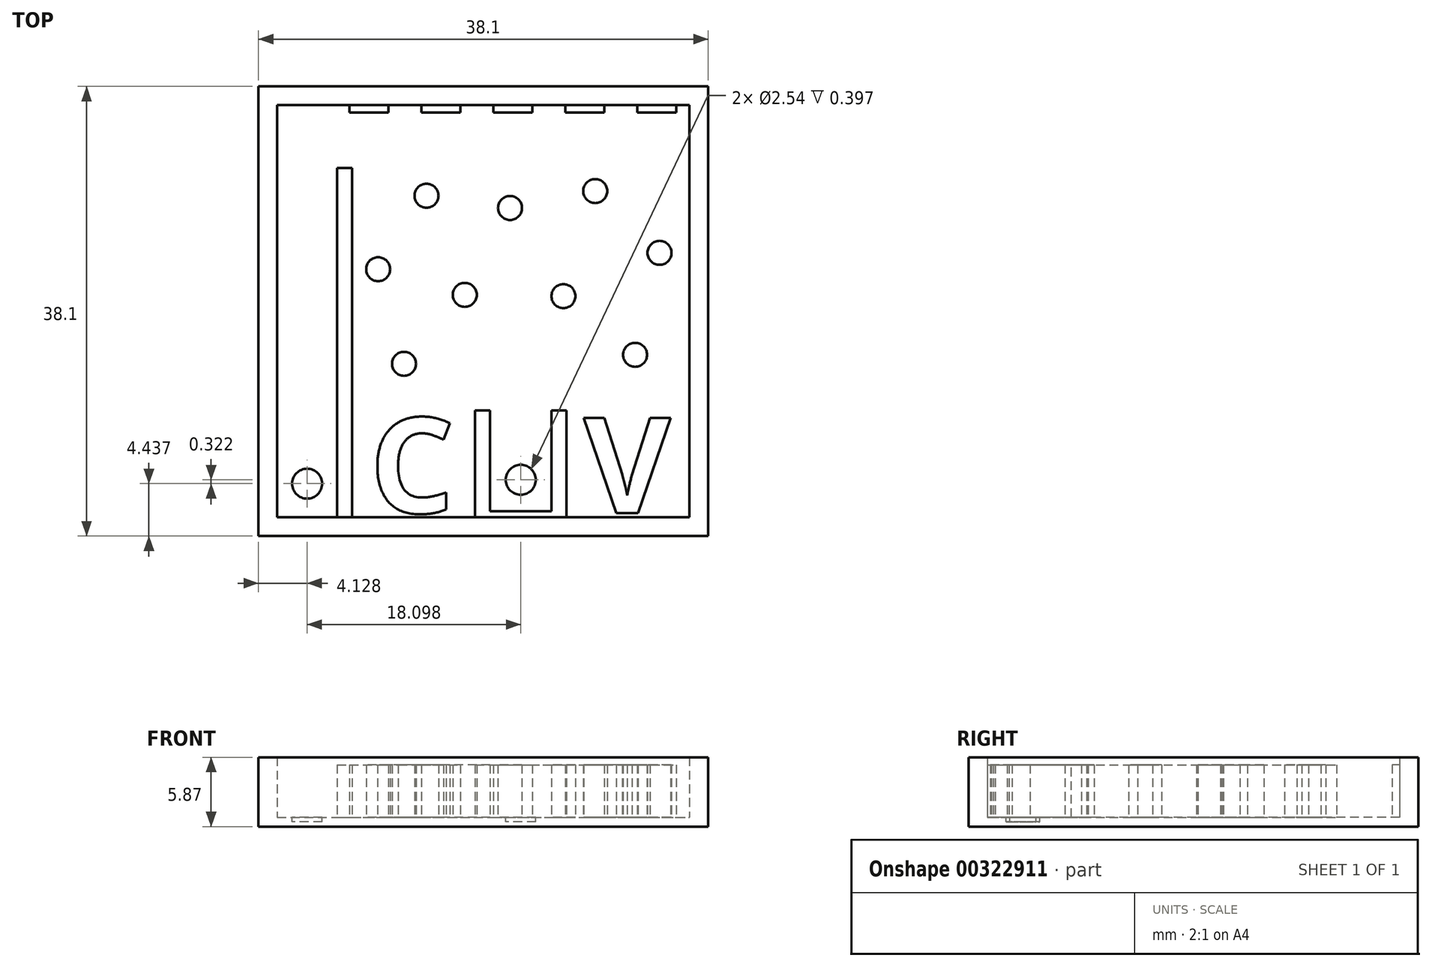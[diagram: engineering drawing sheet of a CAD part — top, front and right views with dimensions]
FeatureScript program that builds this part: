
annotation { "Feature Type Name" : "Feature", "Feature Type Description" : "" }
export const myFeature = defineFeature(function(context is Context, id is Id, definition is map)
    precondition{}
    {
        {
            var Q0;
            Q0=qCreatedBy(makeId("Top.planeOp"),FACE);
            var sketch = newSketch(context, id + "F0", { "sketchPlane" : qUnion([Q0])});
            skLineSegment(sketch, "E0.bottom", {"start": v(-19.05, 22.12) * mm, "end": v(19.05, 22.12) * mm});
            skLineSegment(sketch, "E0.top", {"start": v(-19.05, -15.98) * mm, "end": v(19.05, -15.98) * mm});
            skLineSegment(sketch, "E0.left", {"start": v(-19.05, 22.12) * mm, "end": v(-19.05, -15.98) * mm});
            skLineSegment(sketch, "E0.right", {"start": v(19.05, 22.12) * mm, "end": v(19.05, -15.98) * mm});
            skSolve(sketch);
        }
        {
            var Q0;
            Q0=makeQuery(id+"F0.imprint","IMPRINT",FACE,{"disambiguationData":[TD([[makeQuery(id+"F0.imprint","IMPRINT",EDGE,{"derivedFrom":sQuery(id+"F0.wireOp",EDGE,"E0.bottom")}),-1.0]])]});
            extrude(context, id + "F1", {"entities" : qUnion([Q0]), "depth" : 0.8 * mm});
        }
        {
            var Q0;
            Q0=makeQuery(id+"F1.opExtrude","CAP_FACE",FACE,{"disambiguationData":[OSD([sQuery(id+"F0.wireOp",EDGE,"E0.bottom"),sQuery(id+"F0.wireOp",EDGE,"E0.top"),sQuery(id+"F0.wireOp",EDGE,"E0.left"),sQuery(id+"F0.wireOp",EDGE,"E0.right")])],"isStart":false});
            var sketch = newSketch(context, id + "F2", { "sketchPlane" : qUnion([Q0])});
            skLineSegment(sketch, "E1.0", {"start": v(-17.46, 20.53) * mm, "end": v(17.46, 20.53) * mm});
            skLineSegment(sketch, "E1.1", {"start": v(-17.46, 20.53) * mm, "end": v(-17.46, -14.4) * mm});
            skLineSegment(sketch, "E1.2", {"start": v(-17.46, -14.4) * mm, "end": v(17.46, -14.4) * mm});
            skLineSegment(sketch, "E1.3", {"start": v(17.46, 20.53) * mm, "end": v(17.46, -14.4) * mm});
            skSolve(sketch);
        }
        {
            var Q0;
            Q0=makeQuery(id+"F2.imprint","IMPRINT",FACE,{"disambiguationData":[TD([[makeQuery(id+"F2.imprint","IMPRINT",EDGE,{"derivedFrom":sQuery(id+"F2.wireOp",EDGE,"E1.0")}),1.0]])]});
            extrude(context, id + "F3", {"entities" : qUnion([Q0]), "operationType" : NewBodyOperationType.ADD, "depth" : 5.08 * mm});
        }
        {
            var Q0;
            Q0=makeQuery(id+"F1.opExtrude","CAP_FACE",FACE,{"disambiguationData":[OSD([sQuery(id+"F0.wireOp",EDGE,"E0.bottom"),sQuery(id+"F0.wireOp",EDGE,"E0.top"),sQuery(id+"F0.wireOp",EDGE,"E0.left"),sQuery(id+"F0.wireOp",EDGE,"E0.right")])],"isStart":false});
            var sketch = newSketch(context, id + "F4", { "sketchPlane" : qUnion([Q0])});
            skLineSegment(sketch, "E2.bottom", {"start": v(-12.38, -14.4) * mm, "end": v(-11.11, -14.4) * mm});
            skLineSegment(sketch, "E2.top", {"start": v(-12.38, 15.2) * mm, "end": v(-11.11, 15.2) * mm});
            skLineSegment(sketch, "E2.left", {"start": v(-12.38, -14.4) * mm, "end": v(-12.38, 15.2) * mm});
            skLineSegment(sketch, "E2.right", {"start": v(-11.11, -14.4) * mm, "end": v(-11.11, 15.2) * mm});
            skLineSegment(sketch, "E3", {"start": v(-17.46, -14.4) * mm, "end": v(-12.38, -14.4) * mm});
            skCircle(sketch, "E4", {"center": v(-14.92, -11.54) * mm, "radius": 1.27 * mm});
            skPoint(sketch, "E4.centerSnap0", {"position": v(-14.92, -14.4) * mm});
            skLineSegment(sketch, "E5.bottom", {"start": v(0.85, 20.53) * mm, "end": v(4.15, 20.53) * mm});
            skLineSegment(sketch, "E5.top", {"start": v(0.85, 19.9) * mm, "end": v(4.15, 19.9) * mm});
            skLineSegment(sketch, "E5.left", {"start": v(0.85, 20.53) * mm, "end": v(0.85, 19.9) * mm});
            skLineSegment(sketch, "E5.right", {"start": v(4.15, 20.53) * mm, "end": v(4.15, 19.9) * mm});
            skLineSegment(sketch, "E6.bottom", {"start": v(-5.24, 20.53) * mm, "end": v(-1.94, 20.53) * mm});
            skLineSegment(sketch, "E6.top", {"start": v(-5.24, 19.9) * mm, "end": v(-1.94, 19.9) * mm});
            skLineSegment(sketch, "E6.left", {"start": v(-5.24, 20.53) * mm, "end": v(-5.24, 19.9) * mm});
            skLineSegment(sketch, "E6.right", {"start": v(-1.94, 20.53) * mm, "end": v(-1.94, 19.9) * mm});
            skLineSegment(sketch, "E7.bottom", {"start": v(6.95, 20.53) * mm, "end": v(10.25, 20.53) * mm});
            skLineSegment(sketch, "E7.top", {"start": v(6.95, 19.9) * mm, "end": v(10.25, 19.9) * mm});
            skLineSegment(sketch, "E7.left", {"start": v(6.95, 20.53) * mm, "end": v(6.95, 19.9) * mm});
            skLineSegment(sketch, "E7.right", {"start": v(10.25, 20.53) * mm, "end": v(10.25, 19.9) * mm});
            skLineSegment(sketch, "E8.bottom", {"start": v(13.04, 20.53) * mm, "end": v(16.35, 20.53) * mm});
            skLineSegment(sketch, "E8.top", {"start": v(13.04, 19.9) * mm, "end": v(16.35, 19.9) * mm});
            skLineSegment(sketch, "E8.left", {"start": v(13.04, 20.53) * mm, "end": v(13.04, 19.9) * mm});
            skLineSegment(sketch, "E8.right", {"start": v(16.35, 20.53) * mm, "end": v(16.35, 19.9) * mm});
            skLineSegment(sketch, "E9.bottom", {"start": v(-11.34, 20.53) * mm, "end": v(-8.04, 20.53) * mm});
            skLineSegment(sketch, "E9.top", {"start": v(-11.34, 19.9) * mm, "end": v(-8.04, 19.9) * mm});
            skLineSegment(sketch, "E9.left", {"start": v(-11.34, 20.53) * mm, "end": v(-11.34, 19.9) * mm});
            skLineSegment(sketch, "E9.right", {"start": v(-8.04, 20.53) * mm, "end": v(-8.04, 19.9) * mm});
            skText(sketch, "E10", { "text": "C", "fontName": "OpenSans-Bold.ttf"});
            skText(sketch, "E11", { "text": "V", "fontName": "OpenSans-Bold.ttf"});
            skPoint(sketch, "E12.endSnap0", {"position": v(0, -14.4) * mm});
            skLineSegment(sketch, "E13.bottom", {"start": v(5.78, -14.4) * mm, "end": v(7.05, -14.4) * mm});
            skLineSegment(sketch, "E13.top", {"start": v(5.78, -5.33) * mm, "end": v(7.05, -5.33) * mm});
            skLineSegment(sketch, "E13.left", {"start": v(5.78, -14.4) * mm, "end": v(5.78, -5.33) * mm});
            skLineSegment(sketch, "E13.right", {"start": v(7.05, -14.4) * mm, "end": v(7.05, -5.33) * mm});
            skCircle(sketch, "E14", {"center": v(3.18, -11.22) * mm, "radius": 1.27 * mm});
            skCircle(sketch, "E15", {"center": v(-4.81, 12.85) * mm, "radius": 1.02 * mm});
            skCircle(sketch, "E16", {"center": v(2.27, 11.82) * mm, "radius": 1.02 * mm});
            skCircle(sketch, "E17", {"center": v(9.48, 13.25) * mm, "radius": 1.02 * mm});
            skCircle(sketch, "E18", {"center": v(14.93, 8.01) * mm, "radius": 1.02 * mm});
            skCircle(sketch, "E19", {"center": v(-8.9, 6.63) * mm, "radius": 1.02 * mm});
            skCircle(sketch, "E20", {"center": v(-1.57, 4.46) * mm, "radius": 1.02 * mm});
            skCircle(sketch, "E21", {"center": v(6.79, 4.34) * mm, "radius": 1.02 * mm});
            skLineSegment(sketch, "E22.bottom", {"start": v(0.57, -5.33) * mm, "end": v(-0.7, -5.33) * mm});
            skLineSegment(sketch, "E22.top", {"start": v(0.57, -14.4) * mm, "end": v(-0.7, -14.4) * mm});
            skLineSegment(sketch, "E22.left", {"start": v(0.57, -5.33) * mm, "end": v(0.57, -14.4) * mm});
            skLineSegment(sketch, "E22.right", {"start": v(-0.7, -5.33) * mm, "end": v(-0.7, -14.4) * mm});
            skLineSegment(sketch, "E23.bottom", {"start": v(0.57, -14.4) * mm, "end": v(5.78, -14.4) * mm});
            skLineSegment(sketch, "E23.top", {"start": v(0.57, -13.89) * mm, "end": v(5.78, -13.89) * mm});
            skLineSegment(sketch, "E23.left", {"start": v(0.57, -14.4) * mm, "end": v(0.57, -13.89) * mm});
            skLineSegment(sketch, "E23.right", {"start": v(5.78, -14.4) * mm, "end": v(5.78, -13.89) * mm});
            skCircle(sketch, "E24", {"center": v(12.86, -0.63) * mm, "radius": 1.02 * mm});
            skPoint(sketch, "E25.endSnap0", {"position": v(14.7, 19.9) * mm});
            skCircle(sketch, "E26", {"center": v(-6.72, -1.4) * mm, "radius": 1.02 * mm});
            const initialGuessF4  = {"E10": [-0.00963, -0.01403, 1, 0, 0.00813], "E11": [0.00852, -0.01403, 1, 0, 0.00813]};
            skSetInitialGuess(sketch, initialGuessF4);
            skSolve(sketch);
        }
        {
            var Q0;
            Q0=makeQuery(id+"F4.imprint","IMPRINT",FACE,{"disambiguationData":[TD([[makeQuery(id+"F4.imprint","IMPRINT",EDGE,{"derivedFrom":sQuery(id+"F4.wireOp",EDGE,"E4")}),1.0]])]});
            var Q1;
            Q1=makeQuery(id+"F4.imprint","IMPRINT",FACE,{"disambiguationData":[TD([[makeQuery(id+"F4.imprint","IMPRINT",EDGE,{"derivedFrom":sQuery(id+"F4.wireOp",EDGE,"E14")}),1.0]])]});
            var Q2;
            {var subQ0=sQuery(id+"F4.wireOp",EDGE,"E14");var subQ1=sQuery(id+"F4.wireOp",EDGE,"E12");var subQ2=makeQuery(id+"F4.imprint","INTERSECT",VERTEX,{"disambiguationData":[OD(0.0)],"derivedFrom":[subQ1,subQ0]});Q2=makeQuery(id+"F4.imprint","IMPRINT",FACE,{"disambiguationData":[TD([[makeQuery(id+"F4.imprint","IMPRINT",EDGE,{"disambiguationData":[TD([[subQ2,-1.0]])],"derivedFrom":subQ1}),1.0]])]});}
            var Q3;
            {var subQ0=sQuery(id+"F4.wireOp",EDGE,"E14");var subQ1=sQuery(id+"F4.wireOp",EDGE,"Font8BTO-rPXh-HUv9-cvXY-GG9v0Sla35Q1");var subQ2=makeQuery(id+"F4.imprint","INTERSECT",VERTEX,{"disambiguationData":[OD(0.0)],"derivedFrom":[subQ1,subQ0]});Q3=makeQuery(id+"F4.imprint","IMPRINT",FACE,{"disambiguationData":[TD([[makeQuery(id+"F4.imprint","IMPRINT",EDGE,{"disambiguationData":[TD([[subQ2,-1.0]])],"derivedFrom":subQ1}),1.0]])]});}
            extrude(context, id + "F5", {"entities" : qUnion([Q0, Q1, Q2, Q3]), "operationType" : NewBodyOperationType.REMOVE, "oppositeDirection" : true, "depth" : 0.4 * mm});
        }
        {
            var Q0;
            Q0=makeQuery(id+"F4.imprint","IMPRINT",FACE,{"disambiguationData":[TD([[makeQuery(id+"F4.imprint","IMPRINT",EDGE,{"derivedFrom":sQuery(id+"F4.wireOp",EDGE,"E2.bottom")}),1.0]])]});
            var Q1;
            Q1=makeQuery(id+"F4.imprint","IMPRINT",FACE,{"disambiguationData":[TD([[makeQuery(id+"F4.imprint","IMPRINT",EDGE,{"derivedFrom":sQuery(id+"F4.wireOp",EDGE,"E9.bottom")}),-1.0]])]});
            var Q2;
            Q2=makeQuery(id+"F4.imprint","IMPRINT",FACE,{"disambiguationData":[TD([[makeQuery(id+"F4.imprint","IMPRINT",EDGE,{"derivedFrom":sQuery(id+"F4.wireOp",EDGE,"E6.bottom")}),-1.0]])]});
            var Q3;
            Q3=makeQuery(id+"F4.imprint","IMPRINT",FACE,{"disambiguationData":[TD([[makeQuery(id+"F4.imprint","IMPRINT",EDGE,{"derivedFrom":sQuery(id+"F4.wireOp",EDGE,"E5.bottom")}),-1.0]])]});
            var Q4;
            Q4=makeQuery(id+"F4.imprint","IMPRINT",FACE,{"disambiguationData":[TD([[makeQuery(id+"F4.imprint","IMPRINT",EDGE,{"derivedFrom":sQuery(id+"F4.wireOp",EDGE,"E7.bottom")}),-1.0]])]});
            var Q5;
            Q5=makeQuery(id+"F4.imprint","IMPRINT",FACE,{"disambiguationData":[TD([[makeQuery(id+"F4.imprint","IMPRINT",EDGE,{"derivedFrom":sQuery(id+"F4.wireOp",EDGE,"E8.bottom")}),-1.0]])]});
            var Q6;
            Q6=makeQuery(id+"F4.imprint","IMPRINT",FACE,{"disambiguationData":[TD([[makeQuery(id+"F4.imprint","IMPRINT",EDGE,{"derivedFrom":sQuery(id+"F4.wireOp",EDGE,"E13.bottom")}),1.0]])]});
            var Q7;
            Q7=makeQuery(id+"F4.imprint","IMPRINT",FACE,{"disambiguationData":[TD([[makeQuery(id+"F4.imprint","IMPRINT",EDGE,{"derivedFrom":sQuery(id+"F4.wireOp",EDGE,"E10.sketch_text.stroke-0")}),-1.0]])]});
            var Q8;
            Q8=makeQuery(id+"F4.imprint","IMPRINT",FACE,{"disambiguationData":[TD([[makeQuery(id+"F4.imprint","IMPRINT",EDGE,{"derivedFrom":sQuery(id+"F4.wireOp",EDGE,"E11.sketch_text.stroke-0")}),-1.0]])]});
            var Q9;
            Q9=makeQuery(id+"F4.imprint","IMPRINT",FACE,{"disambiguationData":[TD([[makeQuery(id+"F4.imprint","IMPRINT",EDGE,{"derivedFrom":sQuery(id+"F4.wireOp",EDGE,"E15")}),1.0]])]});
            var Q10;
            Q10=makeQuery(id+"F4.imprint","IMPRINT",FACE,{"disambiguationData":[TD([[makeQuery(id+"F4.imprint","IMPRINT",EDGE,{"derivedFrom":sQuery(id+"F4.wireOp",EDGE,"E19")}),1.0]])]});
            var Q11;
            {var subQ0=sQuery(id+"F4.wireOp",EDGE,"E17");var subQ1=makeQuery(id+"F4.imprint","IMPRINT",VERTEX,{"disambiguationData":[OD(0.0)],"derivedFrom":subQ0});Q11=makeQuery(id+"F4.imprint","IMPRINT",FACE,{"disambiguationData":[TD([[makeQuery(id+"F4.imprint","IMPRINT",EDGE,{"disambiguationData":[TD([[subQ1,-1.0]])],"derivedFrom":subQ0}),1.0]])]});}
            var Q12;
            Q12=makeQuery(id+"F4.imprint","IMPRINT",FACE,{"disambiguationData":[TD([[makeQuery(id+"F4.imprint","IMPRINT",EDGE,{"derivedFrom":sQuery(id+"F4.wireOp",EDGE,"E18")}),1.0]])]});
            var Q13;
            {var subQ0=sQuery(id+"F4.wireOp",EDGE,"E20");var subQ1=makeQuery(id+"F4.imprint","IMPRINT",VERTEX,{"disambiguationData":[OD(0.0)],"derivedFrom":subQ0});Q13=makeQuery(id+"F4.imprint","IMPRINT",FACE,{"disambiguationData":[TD([[makeQuery(id+"F4.imprint","IMPRINT",EDGE,{"disambiguationData":[TD([[subQ1,-1.0]])],"derivedFrom":subQ0}),1.0]])]});}
            var Q14;
            Q14=makeQuery(id+"F4.imprint","IMPRINT",FACE,{"disambiguationData":[TD([[makeQuery(id+"F4.imprint","IMPRINT",EDGE,{"derivedFrom":sQuery(id+"F4.wireOp",EDGE,"E22.bottom")}),1.0]])]});
            var Q15;
            Q15=makeQuery(id+"F4.imprint","IMPRINT",FACE,{"disambiguationData":[TD([[makeQuery(id+"F4.imprint","IMPRINT",EDGE,{"derivedFrom":sQuery(id+"F4.wireOp",EDGE,"E23.bottom")}),1.0]])]});
            var Q16;
            Q16=makeQuery(id+"F4.imprint","IMPRINT",FACE,{"disambiguationData":[TD([[makeQuery(id+"F4.imprint","IMPRINT",EDGE,{"derivedFrom":sQuery(id+"F4.wireOp",EDGE,"E16")}),1.0]])]});
            var Q17;
            Q17=makeQuery(id+"F4.imprint","IMPRINT",FACE,{"disambiguationData":[TD([[makeQuery(id+"F4.imprint","IMPRINT",EDGE,{"derivedFrom":sQuery(id+"F4.wireOp",EDGE,"E17")}),1.0]])]});
            var Q18;
            Q18=makeQuery(id+"F4.imprint","IMPRINT",FACE,{"disambiguationData":[TD([[makeQuery(id+"F4.imprint","IMPRINT",EDGE,{"derivedFrom":sQuery(id+"F4.wireOp",EDGE,"E21")}),1.0]])]});
            var Q19;
            Q19=makeQuery(id+"F4.imprint","IMPRINT",FACE,{"disambiguationData":[TD([[makeQuery(id+"F4.imprint","IMPRINT",EDGE,{"derivedFrom":sQuery(id+"F4.wireOp",EDGE,"E24")}),1.0]])]});
            var Q20;
            Q20=makeQuery(id+"F4.imprint","IMPRINT",FACE,{"disambiguationData":[TD([[makeQuery(id+"F4.imprint","IMPRINT",EDGE,{"derivedFrom":sQuery(id+"F4.wireOp",EDGE,"E20")}),1.0]])]});
            var Q21;
            Q21=makeQuery(id+"F4.imprint","IMPRINT",FACE,{"disambiguationData":[TD([[makeQuery(id+"F4.imprint","IMPRINT",EDGE,{"derivedFrom":sQuery(id+"F4.wireOp",EDGE,"E26")}),1.0]])]});
            extrude(context, id + "F6", {"entities" : qUnion([Q0, Q1, Q2, Q3, Q4, Q5, Q6, Q7, Q8, Q9, Q10, Q11, Q12, Q13, Q14, Q15, Q16, Q17, Q18, Q19, Q20, Q21]), "operationType" : NewBodyOperationType.ADD, "depth" : 4.44 * mm});
        }
    });
